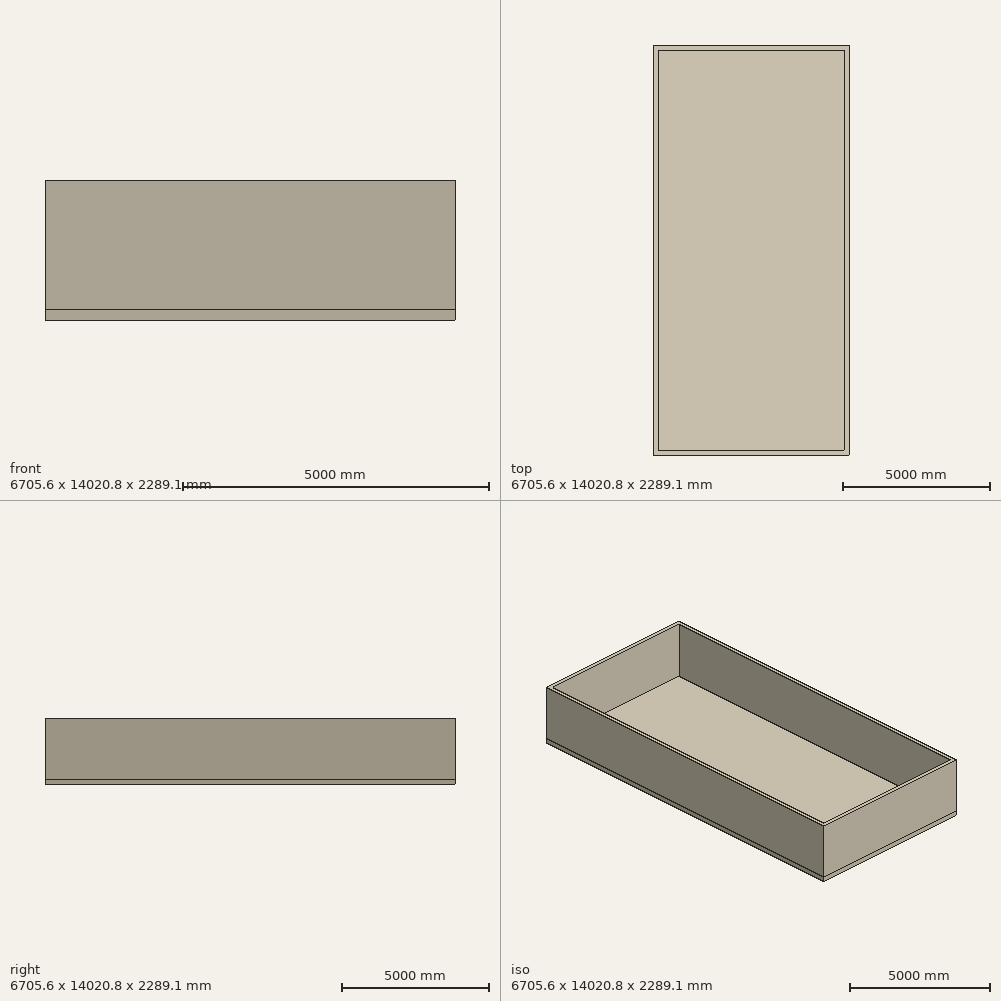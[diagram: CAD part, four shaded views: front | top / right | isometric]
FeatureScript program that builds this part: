
annotation { "Feature Type Name" : "Feature", "Feature Type Description" : "" }
export const myFeature = defineFeature(function(context is Context, id is Id, definition is map)
    precondition{}
    {
        {
            var Q0;
            Q0=qCreatedBy(makeId("Top.planeOp"),FACE);
            var sketch = newSketch(context, id + "F0", { "sketchPlane" : qUnion([Q0])});
            skLineSegment(sketch, "E0.bottom", {"start": v(0, 0) * mm, "end": v(6705.6, 0) * mm});
            skLineSegment(sketch, "E0.top", {"start": v(0, 14020.8) * mm, "end": v(6705.6, 14020.8) * mm});
            skLineSegment(sketch, "E0.left", {"start": v(0, 0) * mm, "end": v(0, 14020.8) * mm});
            skLineSegment(sketch, "E0.right", {"start": v(6705.6, 0) * mm, "end": v(6705.6, 14020.8) * mm});
            skSolve(sketch);
        }
        {
            var Q0;
            Q0 = qSketchRegion(id + "F0", true);
            extrude(context, id + "F1", {"entities" : qUnion([Q0]), "depth" : 30.48 * mm, "offsetDistance" : 30.48 * mm});
        }
        {
            var Q0;
            Q0=makeQuery(id+"F1.opExtrude","CAP_FACE",FACE,{"disambiguationData":[OSD([sQuery(id+"F0.wireOp",EDGE,"E0.bottom"),sQuery(id+"F0.wireOp",EDGE,"E0.top"),sQuery(id+"F0.wireOp",EDGE,"E0.left"),sQuery(id+"F0.wireOp",EDGE,"E0.right")])],"isStart":false});
            shell(context, id + "F2", {"entities" : qUnion([Q0]), "thickness" : 3.05 * mm});
        }
        {
            var Q0;
            Q0=makeQuery(id+"F2.opShell","OFFSET_FACE",FACE,{"disambiguationData":[OSD([sQuery(id+"F0.wireOp",EDGE,"E0.bottom"),sQuery(id+"F0.wireOp",EDGE,"E0.top"),sQuery(id+"F0.wireOp",EDGE,"E0.left"),sQuery(id+"F0.wireOp",EDGE,"E0.right")])]});
            extrude(context, id + "F3", {"entities" : qUnion([Q0]), "operationType" : NewBodyOperationType.ADD, "depth" : 2133.6 * mm, "offsetDistance" : 30.48 * mm});
        }
        {
            var Q0;
            Q0=makeQuery(id+"F1.opExtrude","CAP_FACE",FACE,{"disambiguationData":[OSD([sQuery(id+"F0.wireOp",EDGE,"E0.bottom"),sQuery(id+"F0.wireOp",EDGE,"E0.top"),sQuery(id+"F0.wireOp",EDGE,"E0.left"),sQuery(id+"F0.wireOp",EDGE,"E0.right")])],"isStart":true});
            var Q1;
            Q1=makeQuery(id+"F3.opExtrude","CAP_FACE",FACE,{"disambiguationData":[OSD([sQuery(id+"F0.wireOp",EDGE,"E0.bottom"),sQuery(id+"F0.wireOp",EDGE,"E0.top"),sQuery(id+"F0.wireOp",EDGE,"E0.left"),sQuery(id+"F0.wireOp",EDGE,"E0.right")])],"isStart":false});
            shell(context, id + "F4", {"entities" : qUnion([Q0, Q1]), "thickness" : 152.4 * mm});
        }
        {
            var Q0;
            Q0=makeQuery(id+"F1.opExtrude","CAP_FACE",FACE,{"disambiguationData":[OSD([sQuery(id+"F0.wireOp",EDGE,"E0.bottom"),sQuery(id+"F0.wireOp",EDGE,"E0.top"),sQuery(id+"F0.wireOp",EDGE,"E0.left"),sQuery(id+"F0.wireOp",EDGE,"E0.right")])],"isStart":true});
            var sketch = newSketch(context, id + "F5", { "sketchPlane" : qUnion([Q0])});
            skLineSegment(sketch, "E1.bottom", {"start": v(0, 0) * mm, "end": v(6705.6, 0) * mm});
            skLineSegment(sketch, "E1.top", {"start": v(0, -14020.8) * mm, "end": v(6705.6, -14020.8) * mm});
            skLineSegment(sketch, "E1.left", {"start": v(0, 0) * mm, "end": v(0, -14020.8) * mm});
            skLineSegment(sketch, "E1.right", {"start": v(6705.6, 0) * mm, "end": v(6705.6, -14020.8) * mm});
            skSolve(sketch);
        }
        {
            var Q0;
            Q0 = qSketchRegion(id + "F5", true);
            extrude(context, id + "F6", {"entities" : qUnion([Q0]), "operationType" : NewBodyOperationType.ADD, "depth" : 152.4 * mm, "offsetDistance" : 30.48 * mm});
        }
    });
